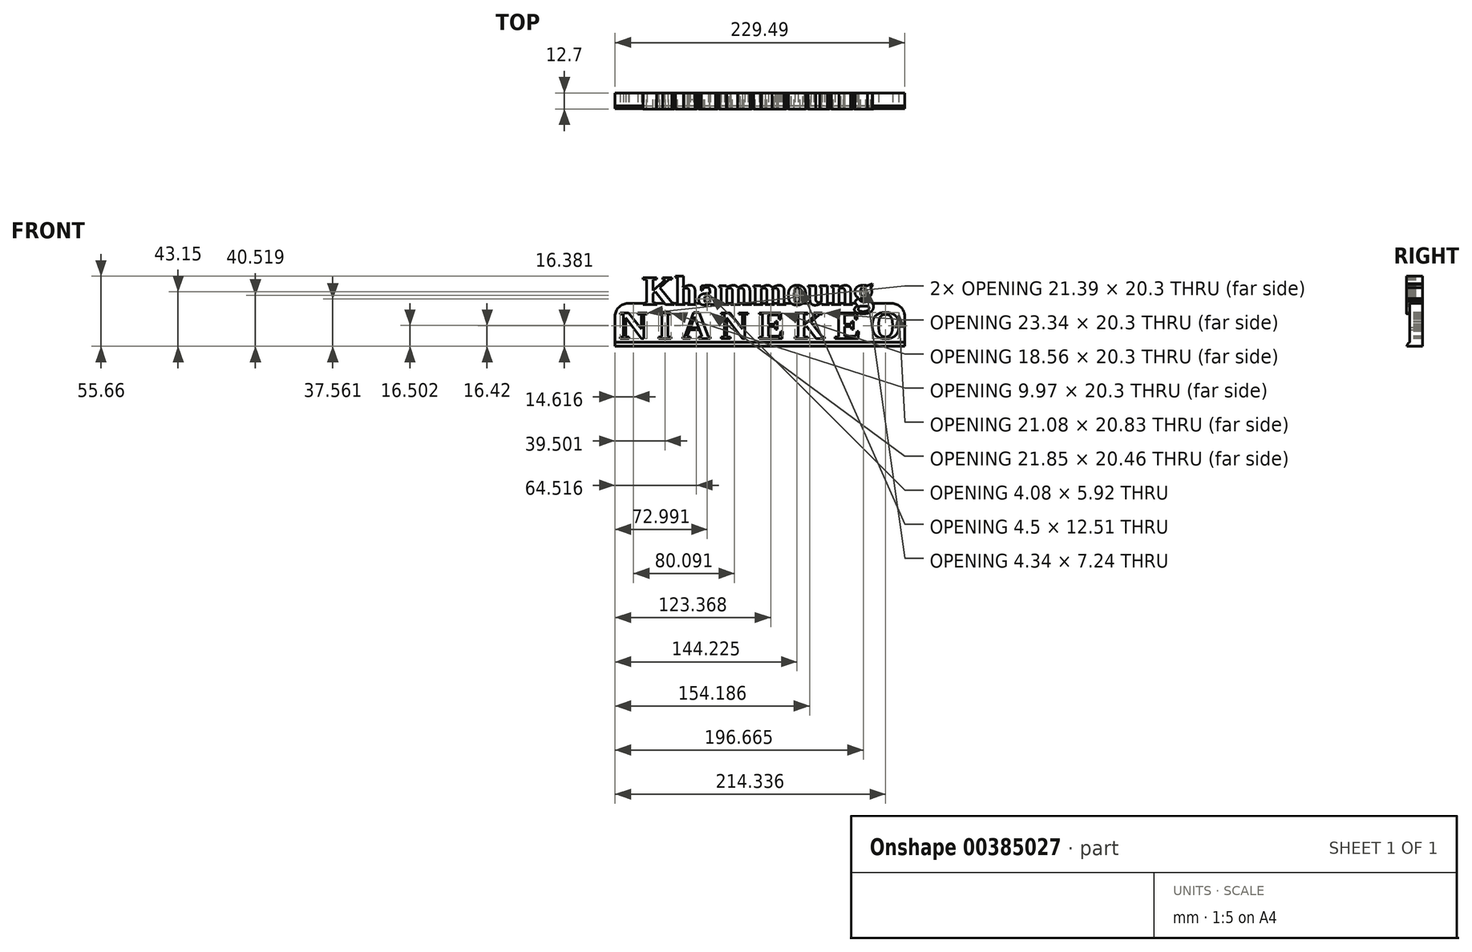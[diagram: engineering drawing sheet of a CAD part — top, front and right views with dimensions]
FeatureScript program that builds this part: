
annotation { "Feature Type Name" : "Feature", "Feature Type Description" : "" }
export const myFeature = defineFeature(function(context is Context, id is Id, definition is map)
    precondition{}
    {
        {
            var Q0;
            Q0=qCreatedBy(makeId("Front.planeOp"),FACE);
            var sketch = newSketch(context, id + "F0", { "sketchPlane" : qUnion([Q0])});
            skLineSegment(sketch, "E0.bottom", {"start": v(-114.42, 5.35) * mm, "end": v(115.07, 5.35) * mm});
            skLineSegment(sketch, "E0.top", {"start": v(-114.42, -28.6) * mm, "end": v(115.07, -28.6) * mm});
            skLineSegment(sketch, "E0.left", {"start": v(-114.42, 5.35) * mm, "end": v(-114.42, -28.6) * mm});
            skLineSegment(sketch, "E0.right", {"start": v(115.07, 5.35) * mm, "end": v(115.07, -28.6) * mm});
            skSolve(sketch);
        }
        {
            var Q0;
            Q0 = qSketchRegion(id + "F0", true);
            extrude(context, id + "F1", {"entities" : qUnion([Q0]), "depth" : 10.16 * mm});
        }
        {
            var Q0;
            Q0=qCreatedBy(makeId("Front.planeOp"),FACE);
            var sketch = newSketch(context, id + "F2", { "sketchPlane" : qUnion([Q0])});
            skText(sketch, "E1", { "text": "Khammoung", "fontName": "Tinos-Bold.ttf"});
            const initialGuessF2  = {"E1": [-0.09269, 0.0044, 1, 0, 0.02352]};
            skSetInitialGuess(sketch, initialGuessF2);
            skSolve(sketch);
        }
        {
            var Q0;
            Q0 = qSketchRegion(id + "F2", true);
            extrude(context, id + "F3", {"entities" : qUnion([Q0]), "operationType" : NewBodyOperationType.ADD, "depth" : 12.7 * mm});
        }
        {
            var Q0;
            {var subQ0=sQuery(id+"F0.wireOp",EDGE,"E0.bottom");var subQ1=sQuery(id+"F0.wireOp",EDGE,"E0.top");var subQ2=sQuery(id+"F0.wireOp",EDGE,"E0.left");var subQ3=sQuery(id+"F0.wireOp",EDGE,"E0.right");Q0=makeQuery(id+"F3.boolean.opBoolean","SPLIT",FACE,{"disambiguationData":[TD([makeQuery(id+"F1.opExtrude","SWEPT_FACE",FACE,{"disambiguationData":[OSD([subQ1])]})])],"derivedFrom":makeQuery(id+"F1.opExtrude","CAP_FACE",FACE,{"disambiguationData":[OSD([subQ0,subQ1,subQ2,subQ3])],"isStart":false})});}
            var sketch = newSketch(context, id + "F4", { "sketchPlane" : qUnion([Q0])});
            skLineSegment(sketch, "E2.bottom", {"start": v(-114.42, -28.6) * mm, "end": v(115.07, -28.6) * mm});
            skLineSegment(sketch, "E2.top", {"start": v(-114.42, -25.32) * mm, "end": v(115.07, -25.32) * mm});
            skLineSegment(sketch, "E2.left", {"start": v(-114.42, -28.6) * mm, "end": v(-114.42, -25.32) * mm});
            skLineSegment(sketch, "E2.right", {"start": v(115.07, -28.6) * mm, "end": v(115.07, -25.32) * mm});
            skSolve(sketch);
        }
        {
            var Q0;
            Q0 = qSketchRegion(id + "F4", true);
            extrude(context, id + "F5", {"entities" : qUnion([Q0]), "operationType" : NewBodyOperationType.ADD, "depth" : 2.54 * mm});
        }
        {
            var Q0;
            Q0=makeQuery(id+"F5.opExtrude","CAP_EDGE",EDGE,{"disambiguationData":[OSD([sQuery(id+"F4.wireOp",EDGE,"E2.top")])],"isStart":false});
            fillet(context, id + "F6", {"entities" : qUnion([Q0]), "radius" : 5.08 * mm, "tangentPropagation" : true, "allowEdgeOverflow" : false});
        }
        {
            var Q0;
            {var subQ0=sQuery(id+"F0.wireOp",EDGE,"E0.bottom");var subQ1=sQuery(id+"F0.wireOp",EDGE,"E0.right");var subQ2=sQuery(id+"F0.wireOp",EDGE,"E0.top");var subQ3=sQuery(id+"F0.wireOp",EDGE,"E0.left");Q0=makeQuery(id+"F3.boolean.opBoolean","SPLIT",FACE,{"disambiguationData":[TD([makeQuery(id+"F1.opExtrude","SWEPT_FACE",FACE,{"disambiguationData":[OSD([subQ2])]})])],"derivedFrom":makeQuery(id+"F1.opExtrude","CAP_FACE",FACE,{"disambiguationData":[OSD([subQ0,subQ2,subQ3,subQ1])],"isStart":false})});}
            var sketch = newSketch(context, id + "F7", { "sketchPlane" : qUnion([Q0])});
            skText(sketch, "E3", { "text": "N I A N E K E O", "fontName": "Tinos-Bold.ttf"});
            const initialGuessF7  = {"E3": [-0.11109, -0.02232, 1, 0, 0.02232]};
            skSetInitialGuess(sketch, initialGuessF7);
            skSolve(sketch);
        }
        {
            var Q0;
            Q0 = qSketchRegion(id + "F7", true);
            var Q1;
            Q1=makeQuery(id+"F3.boolean.opBoolean","MERGE",FACE,{"derivedFrom":[makeQuery(id+"F1.opExtrude","CAP_FACE",FACE,{"disambiguationData":[OSD([sQuery(id+"F0.wireOp",EDGE,"E0.bottom"),sQuery(id+"F0.wireOp",EDGE,"E0.top"),sQuery(id+"F0.wireOp",EDGE,"E0.left"),sQuery(id+"F0.wireOp",EDGE,"E0.right")])],"isStart":true}),makeQuery(id+"F3.opExtrude","CAP_FACE",FACE,{"disambiguationData":[OSD([sQuery(id+"F2.wireOp",EDGE,"E1.sketch_text.stroke-0"),sQuery(id+"F2.wireOp",EDGE,"E1.sketch_text.stroke-1"),sQuery(id+"F2.wireOp",EDGE,"E1.sketch_text.stroke-2"),sQuery(id+"F2.wireOp",EDGE,"E1.sketch_text.stroke-3"),sQuery(id+"F2.wireOp",EDGE,"E1.sketch_text.stroke-4"),sQuery(id+"F2.wireOp",EDGE,"E1.sketch_text.stroke-5"),sQuery(id+"F2.wireOp",EDGE,"E1.sketch_text.stroke-6"),sQuery(id+"F2.wireOp",EDGE,"E1.sketch_text.stroke-7"),sQuery(id+"F2.wireOp",EDGE,"E1.sketch_text.stroke-8"),sQuery(id+"F2.wireOp",EDGE,"E1.sketch_text.stroke-9"),sQuery(id+"F2.wireOp",EDGE,"E1.sketch_text.stroke-10"),sQuery(id+"F2.wireOp",EDGE,"E1.sketch_text.stroke-11"),sQuery(id+"F2.wireOp",EDGE,"E1.sketch_text.stroke-12"),sQuery(id+"F2.wireOp",EDGE,"E1.sketch_text.stroke-13"),sQuery(id+"F2.wireOp",EDGE,"E1.sketch_text.stroke-14"),sQuery(id+"F2.wireOp",EDGE,"E1.sketch_text.stroke-15"),sQuery(id+"F2.wireOp",EDGE,"E1.sketch_text.stroke-16"),sQuery(id+"F2.wireOp",EDGE,"E1.sketch_text.stroke-17"),sQuery(id+"F2.wireOp",EDGE,"E1.sketch_text.stroke-18"),sQuery(id+"F2.wireOp",EDGE,"E1.sketch_text.stroke-19"),sQuery(id+"F2.wireOp",EDGE,"E1.sketch_text.stroke-20"),sQuery(id+"F2.wireOp",EDGE,"E1.sketch_text.stroke-21"),sQuery(id+"F2.wireOp",EDGE,"E1.sketch_text.stroke-22"),sQuery(id+"F2.wireOp",EDGE,"E1.sketch_text.stroke-23"),sQuery(id+"F2.wireOp",EDGE,"E1.sketch_text.stroke-24"),sQuery(id+"F2.wireOp",EDGE,"E1.sketch_text.stroke-25")])],"isStart":true}),makeQuery(id+"F3.opExtrude","CAP_FACE",FACE,{"disambiguationData":[OSD([sQuery(id+"F2.wireOp",EDGE,"E1.sketch_text.stroke-26"),sQuery(id+"F2.wireOp",EDGE,"E1.sketch_text.stroke-27"),sQuery(id+"F2.wireOp",EDGE,"E1.sketch_text.stroke-28"),sQuery(id+"F2.wireOp",EDGE,"E1.sketch_text.stroke-29"),sQuery(id+"F2.wireOp",EDGE,"E1.sketch_text.stroke-30"),sQuery(id+"F2.wireOp",EDGE,"E1.sketch_text.stroke-31"),sQuery(id+"F2.wireOp",EDGE,"E1.sketch_text.stroke-32"),sQuery(id+"F2.wireOp",EDGE,"E1.sketch_text.stroke-33"),sQuery(id+"F2.wireOp",EDGE,"E1.sketch_text.stroke-34"),sQuery(id+"F2.wireOp",EDGE,"E1.sketch_text.stroke-35"),sQuery(id+"F2.wireOp",EDGE,"E1.sketch_text.stroke-36"),sQuery(id+"F2.wireOp",EDGE,"E1.sketch_text.stroke-37"),sQuery(id+"F2.wireOp",EDGE,"E1.sketch_text.stroke-38"),sQuery(id+"F2.wireOp",EDGE,"E1.sketch_text.stroke-39"),sQuery(id+"F2.wireOp",EDGE,"E1.sketch_text.stroke-40"),sQuery(id+"F2.wireOp",EDGE,"E1.sketch_text.stroke-41"),sQuery(id+"F2.wireOp",EDGE,"E1.sketch_text.stroke-42"),sQuery(id+"F2.wireOp",EDGE,"E1.sketch_text.stroke-43"),sQuery(id+"F2.wireOp",EDGE,"E1.sketch_text.stroke-44"),sQuery(id+"F2.wireOp",EDGE,"E1.sketch_text.stroke-45"),sQuery(id+"F2.wireOp",EDGE,"E1.sketch_text.stroke-46"),sQuery(id+"F2.wireOp",EDGE,"E1.sketch_text.stroke-47"),sQuery(id+"F2.wireOp",EDGE,"E1.sketch_text.stroke-48"),sQuery(id+"F2.wireOp",EDGE,"E1.sketch_text.stroke-49"),sQuery(id+"F2.wireOp",EDGE,"E1.sketch_text.stroke-50")])],"isStart":true}),makeQuery(id+"F3.opExtrude","CAP_FACE",FACE,{"disambiguationData":[OSD([sQuery(id+"F2.wireOp",EDGE,"E1.sketch_text.stroke-51"),sQuery(id+"F2.wireOp",EDGE,"E1.sketch_text.stroke-52"),sQuery(id+"F2.wireOp",EDGE,"E1.sketch_text.stroke-53"),sQuery(id+"F2.wireOp",EDGE,"E1.sketch_text.stroke-54"),sQuery(id+"F2.wireOp",EDGE,"E1.sketch_text.stroke-55"),sQuery(id+"F2.wireOp",EDGE,"E1.sketch_text.stroke-56"),sQuery(id+"F2.wireOp",EDGE,"E1.sketch_text.stroke-57"),sQuery(id+"F2.wireOp",EDGE,"E1.sketch_text.stroke-58"),sQuery(id+"F2.wireOp",EDGE,"E1.sketch_text.stroke-59"),sQuery(id+"F2.wireOp",EDGE,"E1.sketch_text.stroke-60"),sQuery(id+"F2.wireOp",EDGE,"E1.sketch_text.stroke-61"),sQuery(id+"F2.wireOp",EDGE,"E1.sketch_text.stroke-62"),sQuery(id+"F2.wireOp",EDGE,"E1.sketch_text.stroke-63"),sQuery(id+"F2.wireOp",EDGE,"E1.sketch_text.stroke-64"),sQuery(id+"F2.wireOp",EDGE,"E1.sketch_text.stroke-65"),sQuery(id+"F2.wireOp",EDGE,"E1.sketch_text.stroke-66"),sQuery(id+"F2.wireOp",EDGE,"E1.sketch_text.stroke-67"),sQuery(id+"F2.wireOp",EDGE,"E1.sketch_text.stroke-68"),sQuery(id+"F2.wireOp",EDGE,"E1.sketch_text.stroke-69"),sQuery(id+"F2.wireOp",EDGE,"E1.sketch_text.stroke-70"),sQuery(id+"F2.wireOp",EDGE,"E1.sketch_text.stroke-71"),sQuery(id+"F2.wireOp",EDGE,"E1.sketch_text.stroke-72"),sQuery(id+"F2.wireOp",EDGE,"E1.sketch_text.stroke-73"),sQuery(id+"F2.wireOp",EDGE,"E1.sketch_text.stroke-74"),sQuery(id+"F2.wireOp",EDGE,"E1.sketch_text.stroke-75"),sQuery(id+"F2.wireOp",EDGE,"E1.sketch_text.stroke-76"),sQuery(id+"F2.wireOp",EDGE,"E1.sketch_text.stroke-77"),sQuery(id+"F2.wireOp",EDGE,"E1.sketch_text.stroke-78")])],"isStart":true}),makeQuery(id+"F3.opExtrude","CAP_FACE",FACE,{"disambiguationData":[OSD([sQuery(id+"F2.wireOp",EDGE,"E1.sketch_text.stroke-79"),sQuery(id+"F2.wireOp",EDGE,"E1.sketch_text.stroke-80"),sQuery(id+"F2.wireOp",EDGE,"E1.sketch_text.stroke-81"),sQuery(id+"F2.wireOp",EDGE,"E1.sketch_text.stroke-82"),sQuery(id+"F2.wireOp",EDGE,"E1.sketch_text.stroke-83"),sQuery(id+"F2.wireOp",EDGE,"E1.sketch_text.stroke-84"),sQuery(id+"F2.wireOp",EDGE,"E1.sketch_text.stroke-85"),sQuery(id+"F2.wireOp",EDGE,"E1.sketch_text.stroke-86"),sQuery(id+"F2.wireOp",EDGE,"E1.sketch_text.stroke-87"),sQuery(id+"F2.wireOp",EDGE,"E1.sketch_text.stroke-88"),sQuery(id+"F2.wireOp",EDGE,"E1.sketch_text.stroke-89"),sQuery(id+"F2.wireOp",EDGE,"E1.sketch_text.stroke-90"),sQuery(id+"F2.wireOp",EDGE,"E1.sketch_text.stroke-91"),sQuery(id+"F2.wireOp",EDGE,"E1.sketch_text.stroke-92"),sQuery(id+"F2.wireOp",EDGE,"E1.sketch_text.stroke-93"),sQuery(id+"F2.wireOp",EDGE,"E1.sketch_text.stroke-94"),sQuery(id+"F2.wireOp",EDGE,"E1.sketch_text.stroke-95"),sQuery(id+"F2.wireOp",EDGE,"E1.sketch_text.stroke-96"),sQuery(id+"F2.wireOp",EDGE,"E1.sketch_text.stroke-97"),sQuery(id+"F2.wireOp",EDGE,"E1.sketch_text.stroke-98"),sQuery(id+"F2.wireOp",EDGE,"E1.sketch_text.stroke-99"),sQuery(id+"F2.wireOp",EDGE,"E1.sketch_text.stroke-100"),sQuery(id+"F2.wireOp",EDGE,"E1.sketch_text.stroke-101"),sQuery(id+"F2.wireOp",EDGE,"E1.sketch_text.stroke-102"),sQuery(id+"F2.wireOp",EDGE,"E1.sketch_text.stroke-103"),sQuery(id+"F2.wireOp",EDGE,"E1.sketch_text.stroke-104"),sQuery(id+"F2.wireOp",EDGE,"E1.sketch_text.stroke-105"),sQuery(id+"F2.wireOp",EDGE,"E1.sketch_text.stroke-106"),sQuery(id+"F2.wireOp",EDGE,"E1.sketch_text.stroke-107"),sQuery(id+"F2.wireOp",EDGE,"E1.sketch_text.stroke-108"),sQuery(id+"F2.wireOp",EDGE,"E1.sketch_text.stroke-109"),sQuery(id+"F2.wireOp",EDGE,"E1.sketch_text.stroke-110"),sQuery(id+"F2.wireOp",EDGE,"E1.sketch_text.stroke-111"),sQuery(id+"F2.wireOp",EDGE,"E1.sketch_text.stroke-112"),sQuery(id+"F2.wireOp",EDGE,"E1.sketch_text.stroke-113"),sQuery(id+"F2.wireOp",EDGE,"E1.sketch_text.stroke-114"),sQuery(id+"F2.wireOp",EDGE,"E1.sketch_text.stroke-115")])],"isStart":true}),makeQuery(id+"F3.opExtrude","CAP_FACE",FACE,{"disambiguationData":[OSD([sQuery(id+"F2.wireOp",EDGE,"E1.sketch_text.stroke-116"),sQuery(id+"F2.wireOp",EDGE,"E1.sketch_text.stroke-117"),sQuery(id+"F2.wireOp",EDGE,"E1.sketch_text.stroke-118"),sQuery(id+"F2.wireOp",EDGE,"E1.sketch_text.stroke-119"),sQuery(id+"F2.wireOp",EDGE,"E1.sketch_text.stroke-120"),sQuery(id+"F2.wireOp",EDGE,"E1.sketch_text.stroke-121"),sQuery(id+"F2.wireOp",EDGE,"E1.sketch_text.stroke-122"),sQuery(id+"F2.wireOp",EDGE,"E1.sketch_text.stroke-123"),sQuery(id+"F2.wireOp",EDGE,"E1.sketch_text.stroke-124"),sQuery(id+"F2.wireOp",EDGE,"E1.sketch_text.stroke-125"),sQuery(id+"F2.wireOp",EDGE,"E1.sketch_text.stroke-126"),sQuery(id+"F2.wireOp",EDGE,"E1.sketch_text.stroke-127"),sQuery(id+"F2.wireOp",EDGE,"E1.sketch_text.stroke-128"),sQuery(id+"F2.wireOp",EDGE,"E1.sketch_text.stroke-129"),sQuery(id+"F2.wireOp",EDGE,"E1.sketch_text.stroke-130"),sQuery(id+"F2.wireOp",EDGE,"E1.sketch_text.stroke-131"),sQuery(id+"F2.wireOp",EDGE,"E1.sketch_text.stroke-132"),sQuery(id+"F2.wireOp",EDGE,"E1.sketch_text.stroke-133"),sQuery(id+"F2.wireOp",EDGE,"E1.sketch_text.stroke-134"),sQuery(id+"F2.wireOp",EDGE,"E1.sketch_text.stroke-135"),sQuery(id+"F2.wireOp",EDGE,"E1.sketch_text.stroke-136"),sQuery(id+"F2.wireOp",EDGE,"E1.sketch_text.stroke-137"),sQuery(id+"F2.wireOp",EDGE,"E1.sketch_text.stroke-138"),sQuery(id+"F2.wireOp",EDGE,"E1.sketch_text.stroke-139"),sQuery(id+"F2.wireOp",EDGE,"E1.sketch_text.stroke-140"),sQuery(id+"F2.wireOp",EDGE,"E1.sketch_text.stroke-141"),sQuery(id+"F2.wireOp",EDGE,"E1.sketch_text.stroke-142"),sQuery(id+"F2.wireOp",EDGE,"E1.sketch_text.stroke-143"),sQuery(id+"F2.wireOp",EDGE,"E1.sketch_text.stroke-144"),sQuery(id+"F2.wireOp",EDGE,"E1.sketch_text.stroke-145"),sQuery(id+"F2.wireOp",EDGE,"E1.sketch_text.stroke-146"),sQuery(id+"F2.wireOp",EDGE,"E1.sketch_text.stroke-147"),sQuery(id+"F2.wireOp",EDGE,"E1.sketch_text.stroke-148"),sQuery(id+"F2.wireOp",EDGE,"E1.sketch_text.stroke-149"),sQuery(id+"F2.wireOp",EDGE,"E1.sketch_text.stroke-150"),sQuery(id+"F2.wireOp",EDGE,"E1.sketch_text.stroke-151"),sQuery(id+"F2.wireOp",EDGE,"E1.sketch_text.stroke-152")])],"isStart":true}),makeQuery(id+"F3.opExtrude","CAP_FACE",FACE,{"disambiguationData":[OSD([sQuery(id+"F2.wireOp",EDGE,"E1.sketch_text.stroke-153"),sQuery(id+"F2.wireOp",EDGE,"E1.sketch_text.stroke-154"),sQuery(id+"F2.wireOp",EDGE,"E1.sketch_text.stroke-155"),sQuery(id+"F2.wireOp",EDGE,"E1.sketch_text.stroke-156"),sQuery(id+"F2.wireOp",EDGE,"E1.sketch_text.stroke-157"),sQuery(id+"F2.wireOp",EDGE,"E1.sketch_text.stroke-158"),sQuery(id+"F2.wireOp",EDGE,"E1.sketch_text.stroke-159"),sQuery(id+"F2.wireOp",EDGE,"E1.sketch_text.stroke-160"),sQuery(id+"F2.wireOp",EDGE,"E1.sketch_text.stroke-161"),sQuery(id+"F2.wireOp",EDGE,"E1.sketch_text.stroke-162"),sQuery(id+"F2.wireOp",EDGE,"E1.sketch_text.stroke-163"),sQuery(id+"F2.wireOp",EDGE,"E1.sketch_text.stroke-164"),sQuery(id+"F2.wireOp",EDGE,"E1.sketch_text.stroke-165"),sQuery(id+"F2.wireOp",EDGE,"E1.sketch_text.stroke-166"),sQuery(id+"F2.wireOp",EDGE,"E1.sketch_text.stroke-167"),sQuery(id+"F2.wireOp",EDGE,"E1.sketch_text.stroke-168")])],"isStart":true}),makeQuery(id+"F3.opExtrude","CAP_FACE",FACE,{"disambiguationData":[OSD([sQuery(id+"F2.wireOp",EDGE,"E1.sketch_text.stroke-169"),sQuery(id+"F2.wireOp",EDGE,"E1.sketch_text.stroke-170"),sQuery(id+"F2.wireOp",EDGE,"E1.sketch_text.stroke-171"),sQuery(id+"F2.wireOp",EDGE,"E1.sketch_text.stroke-172"),sQuery(id+"F2.wireOp",EDGE,"E1.sketch_text.stroke-173"),sQuery(id+"F2.wireOp",EDGE,"E1.sketch_text.stroke-174"),sQuery(id+"F2.wireOp",EDGE,"E1.sketch_text.stroke-175"),sQuery(id+"F2.wireOp",EDGE,"E1.sketch_text.stroke-176"),sQuery(id+"F2.wireOp",EDGE,"E1.sketch_text.stroke-177"),sQuery(id+"F2.wireOp",EDGE,"E1.sketch_text.stroke-178"),sQuery(id+"F2.wireOp",EDGE,"E1.sketch_text.stroke-179"),sQuery(id+"F2.wireOp",EDGE,"E1.sketch_text.stroke-180"),sQuery(id+"F2.wireOp",EDGE,"E1.sketch_text.stroke-181"),sQuery(id+"F2.wireOp",EDGE,"E1.sketch_text.stroke-182"),sQuery(id+"F2.wireOp",EDGE,"E1.sketch_text.stroke-183"),sQuery(id+"F2.wireOp",EDGE,"E1.sketch_text.stroke-184"),sQuery(id+"F2.wireOp",EDGE,"E1.sketch_text.stroke-185"),sQuery(id+"F2.wireOp",EDGE,"E1.sketch_text.stroke-186"),sQuery(id+"F2.wireOp",EDGE,"E1.sketch_text.stroke-187"),sQuery(id+"F2.wireOp",EDGE,"E1.sketch_text.stroke-188")])],"isStart":true}),makeQuery(id+"F3.opExtrude","CAP_FACE",FACE,{"disambiguationData":[OSD([sQuery(id+"F2.wireOp",EDGE,"E1.sketch_text.stroke-189"),sQuery(id+"F2.wireOp",EDGE,"E1.sketch_text.stroke-190"),sQuery(id+"F2.wireOp",EDGE,"E1.sketch_text.stroke-191"),sQuery(id+"F2.wireOp",EDGE,"E1.sketch_text.stroke-192"),sQuery(id+"F2.wireOp",EDGE,"E1.sketch_text.stroke-193"),sQuery(id+"F2.wireOp",EDGE,"E1.sketch_text.stroke-194"),sQuery(id+"F2.wireOp",EDGE,"E1.sketch_text.stroke-195"),sQuery(id+"F2.wireOp",EDGE,"E1.sketch_text.stroke-196"),sQuery(id+"F2.wireOp",EDGE,"E1.sketch_text.stroke-197"),sQuery(id+"F2.wireOp",EDGE,"E1.sketch_text.stroke-198"),sQuery(id+"F2.wireOp",EDGE,"E1.sketch_text.stroke-199"),sQuery(id+"F2.wireOp",EDGE,"E1.sketch_text.stroke-200"),sQuery(id+"F2.wireOp",EDGE,"E1.sketch_text.stroke-201"),sQuery(id+"F2.wireOp",EDGE,"E1.sketch_text.stroke-202"),sQuery(id+"F2.wireOp",EDGE,"E1.sketch_text.stroke-203"),sQuery(id+"F2.wireOp",EDGE,"E1.sketch_text.stroke-204"),sQuery(id+"F2.wireOp",EDGE,"E1.sketch_text.stroke-205"),sQuery(id+"F2.wireOp",EDGE,"E1.sketch_text.stroke-206"),sQuery(id+"F2.wireOp",EDGE,"E1.sketch_text.stroke-207"),sQuery(id+"F2.wireOp",EDGE,"E1.sketch_text.stroke-208"),sQuery(id+"F2.wireOp",EDGE,"E1.sketch_text.stroke-209"),sQuery(id+"F2.wireOp",EDGE,"E1.sketch_text.stroke-210"),sQuery(id+"F2.wireOp",EDGE,"E1.sketch_text.stroke-211"),sQuery(id+"F2.wireOp",EDGE,"E1.sketch_text.stroke-212")])],"isStart":true}),makeQuery(id+"F3.opExtrude","CAP_FACE",FACE,{"disambiguationData":[OSD([sQuery(id+"F2.wireOp",EDGE,"E1.sketch_text.stroke-213"),sQuery(id+"F2.wireOp",EDGE,"E1.sketch_text.stroke-214"),sQuery(id+"F2.wireOp",EDGE,"E1.sketch_text.stroke-215"),sQuery(id+"F2.wireOp",EDGE,"E1.sketch_text.stroke-216"),sQuery(id+"F2.wireOp",EDGE,"E1.sketch_text.stroke-217"),sQuery(id+"F2.wireOp",EDGE,"E1.sketch_text.stroke-218"),sQuery(id+"F2.wireOp",EDGE,"E1.sketch_text.stroke-219"),sQuery(id+"F2.wireOp",EDGE,"E1.sketch_text.stroke-220"),sQuery(id+"F2.wireOp",EDGE,"E1.sketch_text.stroke-221"),sQuery(id+"F2.wireOp",EDGE,"E1.sketch_text.stroke-222"),sQuery(id+"F2.wireOp",EDGE,"E1.sketch_text.stroke-223"),sQuery(id+"F2.wireOp",EDGE,"E1.sketch_text.stroke-224"),sQuery(id+"F2.wireOp",EDGE,"E1.sketch_text.stroke-225"),sQuery(id+"F2.wireOp",EDGE,"E1.sketch_text.stroke-226"),sQuery(id+"F2.wireOp",EDGE,"E1.sketch_text.stroke-227"),sQuery(id+"F2.wireOp",EDGE,"E1.sketch_text.stroke-228"),sQuery(id+"F2.wireOp",EDGE,"E1.sketch_text.stroke-229"),sQuery(id+"F2.wireOp",EDGE,"E1.sketch_text.stroke-230"),sQuery(id+"F2.wireOp",EDGE,"E1.sketch_text.stroke-231"),sQuery(id+"F2.wireOp",EDGE,"E1.sketch_text.stroke-232"),sQuery(id+"F2.wireOp",EDGE,"E1.sketch_text.stroke-233"),sQuery(id+"F2.wireOp",EDGE,"E1.sketch_text.stroke-234"),sQuery(id+"F2.wireOp",EDGE,"E1.sketch_text.stroke-235"),sQuery(id+"F2.wireOp",EDGE,"E1.sketch_text.stroke-236"),sQuery(id+"F2.wireOp",EDGE,"E1.sketch_text.stroke-237"),sQuery(id+"F2.wireOp",EDGE,"E1.sketch_text.stroke-238"),sQuery(id+"F2.wireOp",EDGE,"E1.sketch_text.stroke-239"),sQuery(id+"F2.wireOp",EDGE,"E1.sketch_text.stroke-240"),sQuery(id+"F2.wireOp",EDGE,"E1.sketch_text.stroke-241"),sQuery(id+"F2.wireOp",EDGE,"E1.sketch_text.stroke-242"),sQuery(id+"F2.wireOp",EDGE,"E1.sketch_text.stroke-243"),sQuery(id+"F2.wireOp",EDGE,"E1.sketch_text.stroke-244"),sQuery(id+"F2.wireOp",EDGE,"E1.sketch_text.stroke-245"),sQuery(id+"F2.wireOp",EDGE,"E1.sketch_text.stroke-246"),sQuery(id+"F2.wireOp",EDGE,"E1.sketch_text.stroke-247"),sQuery(id+"F2.wireOp",EDGE,"E1.sketch_text.stroke-248"),sQuery(id+"F2.wireOp",EDGE,"E1.sketch_text.stroke-249"),sQuery(id+"F2.wireOp",EDGE,"E1.sketch_text.stroke-250"),sQuery(id+"F2.wireOp",EDGE,"E1.sketch_text.stroke-251"),sQuery(id+"F2.wireOp",EDGE,"E1.sketch_text.stroke-252"),sQuery(id+"F2.wireOp",EDGE,"E1.sketch_text.stroke-253"),sQuery(id+"F2.wireOp",EDGE,"E1.sketch_text.stroke-254")])],"isStart":true})]});
            extrude(context, id + "F8", {"entities" : qUnion([Q0]), "operationType" : NewBodyOperationType.REMOVE, "endBound" : BoundingType.UP_TO_SURFACE, "oppositeDirection" : true, "endBoundEntityFace" : qUnion([Q1]), "depth" : 25.4 * mm});
        }
        {
            var Q0;
            Q0=makeQuery(id+"F1.opExtrude","SWEPT_EDGE",EDGE,{"disambiguationData":[OSD([sQuery(id+"F0.wireOp",EDGE,"E0.bottom"),sQuery(id+"F0.wireOp",EDGE,"E0.left")])]});
            var Q1;
            Q1=makeQuery(id+"F1.opExtrude","SWEPT_EDGE",EDGE,{"disambiguationData":[OSD([sQuery(id+"F0.wireOp",EDGE,"E0.bottom"),sQuery(id+"F0.wireOp",EDGE,"E0.right")])]});
            fillet(context, id + "F9", {"entities" : qUnion([Q0, Q1]), "radius" : 10.16 * mm, "tangentPropagation" : true, "allowEdgeOverflow" : false});
        }
        {
            var Q0;
            {var subQ0=sQuery(id+"F2.wireOp",EDGE,"E1.sketch_text.stroke-238");var subQ1=sQuery(id+"F2.wireOp",EDGE,"E1.sketch_text.stroke-229");var subQ2=sQuery(id+"F2.wireOp",EDGE,"E1.sketch_text.stroke-228");var subQ3=sQuery(id+"F2.wireOp",EDGE,"E1.sketch_text.stroke-227");var subQ4=sQuery(id+"F2.wireOp",EDGE,"E1.sketch_text.stroke-219");var subQ5=sQuery(id+"F2.wireOp",EDGE,"E1.sketch_text.stroke-218");var subQ6=sQuery(id+"F2.wireOp",EDGE,"E1.sketch_text.stroke-217");var subQ7=sQuery(id+"F2.wireOp",EDGE,"E1.sketch_text.stroke-213");var subQ8=sQuery(id+"F2.wireOp",EDGE,"E1.sketch_text.stroke-212");var subQ9=sQuery(id+"F2.wireOp",EDGE,"E1.sketch_text.stroke-198");var subQ10=sQuery(id+"F2.wireOp",EDGE,"E1.sketch_text.stroke-197");var subQ11=sQuery(id+"F2.wireOp",EDGE,"E1.sketch_text.stroke-191");var subQ12=sQuery(id+"F2.wireOp",EDGE,"E1.sketch_text.stroke-190");var subQ13=sQuery(id+"F2.wireOp",EDGE,"E1.sketch_text.stroke-184");var subQ14=sQuery(id+"F2.wireOp",EDGE,"E1.sketch_text.stroke-183");var subQ15=sQuery(id+"F2.wireOp",EDGE,"E1.sketch_text.stroke-182");var subQ16=sQuery(id+"F2.wireOp",EDGE,"E1.sketch_text.stroke-181");var subQ17=sQuery(id+"F2.wireOp",EDGE,"E1.sketch_text.stroke-180");var subQ18=sQuery(id+"F2.wireOp",EDGE,"E1.sketch_text.stroke-179");var subQ19=sQuery(id+"F2.wireOp",EDGE,"E1.sketch_text.stroke-178");var subQ20=sQuery(id+"F2.wireOp",EDGE,"E1.sketch_text.stroke-177");var subQ21=sQuery(id+"F2.wireOp",EDGE,"E1.sketch_text.stroke-176");var subQ22=sQuery(id+"F2.wireOp",EDGE,"E1.sketch_text.stroke-175");var subQ23=sQuery(id+"F2.wireOp",EDGE,"E1.sketch_text.stroke-174");var subQ24=sQuery(id+"F2.wireOp",EDGE,"E1.sketch_text.stroke-173");var subQ25=sQuery(id+"F2.wireOp",EDGE,"E1.sketch_text.stroke-172");var subQ26=sQuery(id+"F2.wireOp",EDGE,"E1.sketch_text.stroke-171");var subQ27=sQuery(id+"F2.wireOp",EDGE,"E1.sketch_text.stroke-169");var subQ28=sQuery(id+"F2.wireOp",EDGE,"E1.sketch_text.stroke-168");var subQ29=sQuery(id+"F2.wireOp",EDGE,"E1.sketch_text.stroke-167");var subQ30=sQuery(id+"F2.wireOp",EDGE,"E1.sketch_text.stroke-166");var subQ31=sQuery(id+"F2.wireOp",EDGE,"E1.sketch_text.stroke-162");var subQ32=sQuery(id+"F2.wireOp",EDGE,"E1.sketch_text.stroke-161");var subQ33=sQuery(id+"F2.wireOp",EDGE,"E1.sketch_text.stroke-159");var subQ34=sQuery(id+"F2.wireOp",EDGE,"E1.sketch_text.stroke-158");var subQ35=sQuery(id+"F2.wireOp",EDGE,"E1.sketch_text.stroke-157");var subQ36=sQuery(id+"F2.wireOp",EDGE,"E1.sketch_text.stroke-156");var subQ37=sQuery(id+"F2.wireOp",EDGE,"E1.sketch_text.stroke-155");var subQ38=sQuery(id+"F2.wireOp",EDGE,"E1.sketch_text.stroke-154");var subQ39=sQuery(id+"F2.wireOp",EDGE,"E1.sketch_text.stroke-153");var subQ40=sQuery(id+"F2.wireOp",EDGE,"E1.sketch_text.stroke-152");var subQ41=sQuery(id+"F2.wireOp",EDGE,"E1.sketch_text.stroke-151");var subQ42=sQuery(id+"F2.wireOp",EDGE,"E1.sketch_text.stroke-150");var subQ43=sQuery(id+"F2.wireOp",EDGE,"E1.sketch_text.stroke-149");var subQ44=sQuery(id+"F2.wireOp",EDGE,"E1.sketch_text.stroke-148");var subQ45=sQuery(id+"F2.wireOp",EDGE,"E1.sketch_text.stroke-147");var subQ46=sQuery(id+"F2.wireOp",EDGE,"E1.sketch_text.stroke-143");var subQ47=sQuery(id+"F2.wireOp",EDGE,"E1.sketch_text.stroke-142");var subQ48=sQuery(id+"F2.wireOp",EDGE,"E1.sketch_text.stroke-141");var subQ49=sQuery(id+"F2.wireOp",EDGE,"E1.sketch_text.stroke-140");var subQ50=sQuery(id+"F2.wireOp",EDGE,"E1.sketch_text.stroke-139");var subQ51=sQuery(id+"F2.wireOp",EDGE,"E1.sketch_text.stroke-138");var subQ52=sQuery(id+"F2.wireOp",EDGE,"E1.sketch_text.stroke-137");var subQ53=sQuery(id+"F2.wireOp",EDGE,"E1.sketch_text.stroke-133");var subQ54=sQuery(id+"F2.wireOp",EDGE,"E1.sketch_text.stroke-132");var subQ55=sQuery(id+"F2.wireOp",EDGE,"E1.sketch_text.stroke-131");var subQ56=sQuery(id+"F2.wireOp",EDGE,"E1.sketch_text.stroke-130");var subQ57=sQuery(id+"F2.wireOp",EDGE,"E1.sketch_text.stroke-129");var subQ58=sQuery(id+"F2.wireOp",EDGE,"E1.sketch_text.stroke-128");var subQ59=sQuery(id+"F2.wireOp",EDGE,"E1.sketch_text.stroke-127");var subQ60=sQuery(id+"F2.wireOp",EDGE,"E1.sketch_text.stroke-126");var subQ61=sQuery(id+"F2.wireOp",EDGE,"E1.sketch_text.stroke-122");var subQ62=sQuery(id+"F2.wireOp",EDGE,"E1.sketch_text.stroke-121");var subQ63=sQuery(id+"F2.wireOp",EDGE,"E1.sketch_text.stroke-120");var subQ64=sQuery(id+"F2.wireOp",EDGE,"E1.sketch_text.stroke-119");var subQ65=sQuery(id+"F2.wireOp",EDGE,"E1.sketch_text.stroke-118");var subQ66=sQuery(id+"F2.wireOp",EDGE,"E1.sketch_text.stroke-117");var subQ67=sQuery(id+"F2.wireOp",EDGE,"E1.sketch_text.stroke-51");var subQ68=sQuery(id+"F2.wireOp",EDGE,"E1.sketch_text.stroke-50");var subQ69=sQuery(id+"F2.wireOp",EDGE,"E1.sketch_text.stroke-45");var subQ70=sQuery(id+"F2.wireOp",EDGE,"E1.sketch_text.stroke-226");var subQ71=sQuery(id+"F2.wireOp",EDGE,"E1.sketch_text.stroke-41");var subQ72=sQuery(id+"F2.wireOp",EDGE,"E1.sketch_text.stroke-225");var subQ73=sQuery(id+"F2.wireOp",EDGE,"E1.sketch_text.stroke-40");var subQ74=sQuery(id+"F2.wireOp",EDGE,"E1.sketch_text.stroke-224");var subQ75=sQuery(id+"F2.wireOp",EDGE,"E1.sketch_text.stroke-39");var subQ76=sQuery(id+"F2.wireOp",EDGE,"E1.sketch_text.stroke-223");var subQ77=sQuery(id+"F2.wireOp",EDGE,"E1.sketch_text.stroke-38");var subQ78=sQuery(id+"F2.wireOp",EDGE,"E1.sketch_text.stroke-222");var subQ79=sQuery(id+"F2.wireOp",EDGE,"E1.sketch_text.stroke-37");var subQ80=sQuery(id+"F2.wireOp",EDGE,"E1.sketch_text.stroke-221");var subQ81=sQuery(id+"F2.wireOp",EDGE,"E1.sketch_text.stroke-36");var subQ82=sQuery(id+"F2.wireOp",EDGE,"E1.sketch_text.stroke-220");var subQ83=sQuery(id+"F2.wireOp",EDGE,"E1.sketch_text.stroke-35");var subQ84=sQuery(id+"F2.wireOp",EDGE,"E1.sketch_text.stroke-216");var subQ85=sQuery(id+"F2.wireOp",EDGE,"E1.sketch_text.stroke-31");var subQ86=sQuery(id+"F2.wireOp",EDGE,"E1.sketch_text.stroke-215");var subQ87=sQuery(id+"F2.wireOp",EDGE,"E1.sketch_text.stroke-30");var subQ88=sQuery(id+"F2.wireOp",EDGE,"E1.sketch_text.stroke-214");var subQ89=sQuery(id+"F2.wireOp",EDGE,"E1.sketch_text.stroke-29");var subQ90=sQuery(id+"F2.wireOp",EDGE,"E1.sketch_text.stroke-28");var subQ91=sQuery(id+"F2.wireOp",EDGE,"E1.sketch_text.stroke-27");var subQ92=sQuery(id+"F2.wireOp",EDGE,"E1.sketch_text.stroke-211");var subQ93=sQuery(id+"F2.wireOp",EDGE,"E1.sketch_text.stroke-26");var subQ94=sQuery(id+"F2.wireOp",EDGE,"E1.sketch_text.stroke-210");var subQ95=sQuery(id+"F2.wireOp",EDGE,"E1.sketch_text.stroke-25");var subQ96=sQuery(id+"F2.wireOp",EDGE,"E1.sketch_text.stroke-116");var subQ97=sQuery(id+"F2.wireOp",EDGE,"E1.sketch_text.stroke-209");var subQ98=sQuery(id+"F2.wireOp",EDGE,"E1.sketch_text.stroke-24");var subQ99=sQuery(id+"F2.wireOp",EDGE,"E1.sketch_text.stroke-115");var subQ100=sQuery(id+"F2.wireOp",EDGE,"E1.sketch_text.stroke-208");var subQ101=sQuery(id+"F2.wireOp",EDGE,"E1.sketch_text.stroke-23");var subQ102=sQuery(id+"F2.wireOp",EDGE,"E1.sketch_text.stroke-114");var subQ103=sQuery(id+"F2.wireOp",EDGE,"E1.sketch_text.stroke-192");var subQ104=sQuery(id+"F2.wireOp",EDGE,"E1.sketch_text.stroke-7");var subQ105=sQuery(id+"F2.wireOp",EDGE,"E1.sketch_text.stroke-49");var subQ106=sQuery(id+"F2.wireOp",EDGE,"E1.sketch_text.stroke-4");var subQ107=sQuery(id+"F2.wireOp",EDGE,"E1.sketch_text.stroke-95");var subQ108=sQuery(id+"F2.wireOp",EDGE,"E1.sketch_text.stroke-48");var subQ109=sQuery(id+"F2.wireOp",EDGE,"E1.sketch_text.stroke-3");var subQ110=sQuery(id+"F2.wireOp",EDGE,"E1.sketch_text.stroke-94");var subQ111=sQuery(id+"F2.wireOp",EDGE,"E1.sketch_text.stroke-185");var subQ112=sQuery(id+"F2.wireOp",EDGE,"E1.sketch_text.stroke-0");var subQ113=sQuery(id+"F2.wireOp",EDGE,"E1.sketch_text.stroke-89");var subQ114=sQuery(id+"F2.wireOp",EDGE,"E1.sketch_text.stroke-164");var subQ115=sQuery(id+"F0.wireOp",EDGE,"E0.left");var subQ116=sQuery(id+"F2.wireOp",EDGE,"E1.sketch_text.stroke-77");var subQ117=sQuery(id+"F2.wireOp",EDGE,"E1.sketch_text.stroke-21");var subQ118=sQuery(id+"F2.wireOp",EDGE,"E1.sketch_text.stroke-112");var subQ119=sQuery(id+"F2.wireOp",EDGE,"E1.sketch_text.stroke-160");var subQ120=sQuery(id+"F0.wireOp",EDGE,"E0.bottom");var subQ121=sQuery(id+"F2.wireOp",EDGE,"E1.sketch_text.stroke-73");var subQ122=sQuery(id+"F2.wireOp",EDGE,"E1.sketch_text.stroke-202");var subQ123=sQuery(id+"F2.wireOp",EDGE,"E1.sketch_text.stroke-17");var subQ124=sQuery(id+"F2.wireOp",EDGE,"E1.sketch_text.stroke-47");var subQ125=sQuery(id+"F2.wireOp",EDGE,"E1.sketch_text.stroke-189");var subQ126=sQuery(id+"F2.wireOp",EDGE,"E1.sketch_text.stroke-2");var subQ127=sQuery(id+"F2.wireOp",EDGE,"E1.sketch_text.stroke-93");var subQ128=sQuery(id+"F2.wireOp",EDGE,"E1.sketch_text.stroke-165");var subQ129=sQuery(id+"F0.wireOp",EDGE,"E0.right");var subQ130=sQuery(id+"F2.wireOp",EDGE,"E1.sketch_text.stroke-78");var subQ131=sQuery(id+"F2.wireOp",EDGE,"E1.sketch_text.stroke-207");var subQ132=sQuery(id+"F2.wireOp",EDGE,"E1.sketch_text.stroke-22");var subQ133=sQuery(id+"F2.wireOp",EDGE,"E1.sketch_text.stroke-113");var subQ134=sQuery(id+"F2.wireOp",EDGE,"E1.sketch_text.stroke-163");var subQ135=sQuery(id+"F0.wireOp",EDGE,"E0.top");var subQ136=sQuery(id+"F2.wireOp",EDGE,"E1.sketch_text.stroke-76");var subQ137=sQuery(id+"F2.wireOp",EDGE,"E1.sketch_text.stroke-20");var subQ138=sQuery(id+"F2.wireOp",EDGE,"E1.sketch_text.stroke-111");var subQ139=sQuery(id+"F2.wireOp",EDGE,"E1.sketch_text.stroke-46");var subQ140=sQuery(id+"F2.wireOp",EDGE,"E1.sketch_text.stroke-188");var subQ141=sQuery(id+"F2.wireOp",EDGE,"E1.sketch_text.stroke-1");var subQ142=sQuery(id+"F2.wireOp",EDGE,"E1.sketch_text.stroke-92");var subQ143=sQuery(id+"F2.wireOp",EDGE,"E1.sketch_text.stroke-193");var subQ144=sQuery(id+"F2.wireOp",EDGE,"E1.sketch_text.stroke-8");var subQ145=sQuery(id+"F2.wireOp",EDGE,"E1.sketch_text.stroke-239");var subQ146=sQuery(id+"F2.wireOp",EDGE,"E1.sketch_text.stroke-52");var subQ147=sQuery(id+"F2.wireOp",EDGE,"E1.sketch_text.stroke-9");var subQ148=sQuery(id+"F2.wireOp",EDGE,"E1.sketch_text.stroke-100");var subQ149=sQuery(id+"F2.wireOp",EDGE,"E1.sketch_text.stroke-10");var subQ150=sQuery(id+"F2.wireOp",EDGE,"E1.sketch_text.stroke-101");var subQ151=sQuery(id+"F2.wireOp",EDGE,"E1.sketch_text.stroke-199");var subQ152=sQuery(id+"F2.wireOp",EDGE,"E1.sketch_text.stroke-14");var subQ153=sQuery(id+"F2.wireOp",EDGE,"E1.sketch_text.stroke-105");var subQ154=sQuery(id+"F2.wireOp",EDGE,"E1.sketch_text.stroke-200");var subQ155=sQuery(id+"F2.wireOp",EDGE,"E1.sketch_text.stroke-15");var subQ156=sQuery(id+"F2.wireOp",EDGE,"E1.sketch_text.stroke-106");var subQ157=sQuery(id+"F2.wireOp",EDGE,"E1.sketch_text.stroke-201");var subQ158=sQuery(id+"F2.wireOp",EDGE,"E1.sketch_text.stroke-16");var subQ159=sQuery(id+"F2.wireOp",EDGE,"E1.sketch_text.stroke-203");var subQ160=sQuery(id+"F2.wireOp",EDGE,"E1.sketch_text.stroke-18");var subQ161=sQuery(id+"F2.wireOp",EDGE,"E1.sketch_text.stroke-19");var subQ162=sQuery(id+"F2.wireOp",EDGE,"E1.sketch_text.stroke-110");var subQ163=sQuery(id+"F2.wireOp",EDGE,"E1.sketch_text.stroke-53");var subQ164=sQuery(id+"F2.wireOp",EDGE,"E1.sketch_text.stroke-59");var subQ165=sQuery(id+"F2.wireOp",EDGE,"E1.sketch_text.stroke-247");var subQ166=sQuery(id+"F2.wireOp",EDGE,"E1.sketch_text.stroke-60");var subQ167=sQuery(id+"F2.wireOp",EDGE,"E1.sketch_text.stroke-248");var subQ168=sQuery(id+"F2.wireOp",EDGE,"E1.sketch_text.stroke-61");var subQ169=sQuery(id+"F2.wireOp",EDGE,"E1.sketch_text.stroke-249");var subQ170=sQuery(id+"F2.wireOp",EDGE,"E1.sketch_text.stroke-62");var subQ171=sQuery(id+"F2.wireOp",EDGE,"E1.sketch_text.stroke-250");var subQ172=sQuery(id+"F2.wireOp",EDGE,"E1.sketch_text.stroke-63");var subQ173=sQuery(id+"F2.wireOp",EDGE,"E1.sketch_text.stroke-251");var subQ174=sQuery(id+"F2.wireOp",EDGE,"E1.sketch_text.stroke-64");var subQ175=sQuery(id+"F2.wireOp",EDGE,"E1.sketch_text.stroke-65");var subQ176=sQuery(id+"F2.wireOp",EDGE,"E1.sketch_text.stroke-66");var subQ177=sQuery(id+"F2.wireOp",EDGE,"E1.sketch_text.stroke-67");var subQ178=sQuery(id+"F2.wireOp",EDGE,"E1.sketch_text.stroke-68");var subQ179=sQuery(id+"F2.wireOp",EDGE,"E1.sketch_text.stroke-69");var subQ180=sQuery(id+"F2.wireOp",EDGE,"E1.sketch_text.stroke-70");var subQ181=sQuery(id+"F2.wireOp",EDGE,"E1.sketch_text.stroke-71");var subQ182=sQuery(id+"F2.wireOp",EDGE,"E1.sketch_text.stroke-72");var subQ183=sQuery(id+"F2.wireOp",EDGE,"E1.sketch_text.stroke-74");var subQ184=sQuery(id+"F2.wireOp",EDGE,"E1.sketch_text.stroke-75");var subQ185=sQuery(id+"F2.wireOp",EDGE,"E1.sketch_text.stroke-79");var subQ186=sQuery(id+"F2.wireOp",EDGE,"E1.sketch_text.stroke-80");var subQ187=sQuery(id+"F2.wireOp",EDGE,"E1.sketch_text.stroke-81");var subQ188=sQuery(id+"F2.wireOp",EDGE,"E1.sketch_text.stroke-82");var subQ189=sQuery(id+"F2.wireOp",EDGE,"E1.sketch_text.stroke-83");var subQ190=sQuery(id+"F2.wireOp",EDGE,"E1.sketch_text.stroke-84");var subQ191=sQuery(id+"F2.wireOp",EDGE,"E1.sketch_text.stroke-85");var subQ192=sQuery(id+"F2.wireOp",EDGE,"E1.sketch_text.stroke-90");var subQ193=sQuery(id+"F2.wireOp",EDGE,"E1.sketch_text.stroke-91");var subQ194=sQuery(id+"F2.wireOp",EDGE,"E1.sketch_text.stroke-96");var subQ195=sQuery(id+"F2.wireOp",EDGE,"E1.sketch_text.stroke-102");var subQ196=sQuery(id+"F2.wireOp",EDGE,"E1.sketch_text.stroke-103");var subQ197=sQuery(id+"F2.wireOp",EDGE,"E1.sketch_text.stroke-104");var subQ198=sQuery(id+"F2.wireOp",EDGE,"E1.sketch_text.stroke-252");var subQ199=sQuery(id+"F2.wireOp",EDGE,"E1.sketch_text.stroke-253");var subQ200=sQuery(id+"F2.wireOp",EDGE,"E1.sketch_text.stroke-254");Q0=makeQuery(id+"F8.boolean.opBoolean","SPLIT",FACE,{"disambiguationData":[TD([makeQuery(id+"F1.opExtrude","SWEPT_FACE",FACE,{"disambiguationData":[OSD([subQ120])]})])],"derivedFrom":makeQuery(id+"F3.boolean.opBoolean","MERGE",FACE,{"derivedFrom":[makeQuery(id+"F1.opExtrude","CAP_FACE",FACE,{"disambiguationData":[OSD([subQ120,subQ135,subQ115,subQ129])],"isStart":true}),makeQuery(id+"F3.opExtrude","CAP_FACE",FACE,{"disambiguationData":[OSD([subQ112,subQ141,subQ126,subQ109,subQ106,sQuery(id+"F2.wireOp",EDGE,"E1.sketch_text.stroke-5"),sQuery(id+"F2.wireOp",EDGE,"E1.sketch_text.stroke-6"),subQ104,subQ144,subQ147,subQ149,sQuery(id+"F2.wireOp",EDGE,"E1.sketch_text.stroke-11"),sQuery(id+"F2.wireOp",EDGE,"E1.sketch_text.stroke-12"),sQuery(id+"F2.wireOp",EDGE,"E1.sketch_text.stroke-13"),subQ152,subQ155,subQ158,subQ123,subQ160,subQ161,subQ137,subQ117,subQ132,subQ101,subQ98,subQ95])],"isStart":true}),makeQuery(id+"F3.opExtrude","CAP_FACE",FACE,{"disambiguationData":[OSD([subQ93,subQ91,subQ90,subQ89,subQ87,subQ85,sQuery(id+"F2.wireOp",EDGE,"E1.sketch_text.stroke-32"),sQuery(id+"F2.wireOp",EDGE,"E1.sketch_text.stroke-33"),sQuery(id+"F2.wireOp",EDGE,"E1.sketch_text.stroke-34"),subQ83,subQ81,subQ79,subQ77,subQ75,subQ73,subQ71,sQuery(id+"F2.wireOp",EDGE,"E1.sketch_text.stroke-42"),sQuery(id+"F2.wireOp",EDGE,"E1.sketch_text.stroke-43"),sQuery(id+"F2.wireOp",EDGE,"E1.sketch_text.stroke-44"),subQ69,subQ139,subQ124,subQ108,subQ105,subQ68])],"isStart":true}),makeQuery(id+"F3.opExtrude","CAP_FACE",FACE,{"disambiguationData":[OSD([subQ67,subQ146,subQ163,sQuery(id+"F2.wireOp",EDGE,"E1.sketch_text.stroke-54"),sQuery(id+"F2.wireOp",EDGE,"E1.sketch_text.stroke-55"),sQuery(id+"F2.wireOp",EDGE,"E1.sketch_text.stroke-56"),sQuery(id+"F2.wireOp",EDGE,"E1.sketch_text.stroke-57"),sQuery(id+"F2.wireOp",EDGE,"E1.sketch_text.stroke-58"),subQ164,subQ166,subQ168,subQ170,subQ172,subQ174,subQ175,subQ176,subQ177,subQ178,subQ179,subQ180,subQ181,subQ182,subQ121,subQ183,subQ184,subQ136,subQ116,subQ130])],"isStart":true}),makeQuery(id+"F3.opExtrude","CAP_FACE",FACE,{"disambiguationData":[OSD([subQ185,subQ186,subQ187,subQ188,subQ189,subQ190,subQ191,sQuery(id+"F2.wireOp",EDGE,"E1.sketch_text.stroke-86"),sQuery(id+"F2.wireOp",EDGE,"E1.sketch_text.stroke-87"),sQuery(id+"F2.wireOp",EDGE,"E1.sketch_text.stroke-88"),subQ113,subQ192,subQ193,subQ142,subQ127,subQ110,subQ107,subQ194,sQuery(id+"F2.wireOp",EDGE,"E1.sketch_text.stroke-97"),sQuery(id+"F2.wireOp",EDGE,"E1.sketch_text.stroke-98"),sQuery(id+"F2.wireOp",EDGE,"E1.sketch_text.stroke-99"),subQ148,subQ150,subQ195,subQ196,subQ197,subQ153,subQ156,sQuery(id+"F2.wireOp",EDGE,"E1.sketch_text.stroke-107"),sQuery(id+"F2.wireOp",EDGE,"E1.sketch_text.stroke-108"),sQuery(id+"F2.wireOp",EDGE,"E1.sketch_text.stroke-109"),subQ162,subQ138,subQ118,subQ133,subQ102,subQ99])],"isStart":true}),makeQuery(id+"F3.opExtrude","CAP_FACE",FACE,{"disambiguationData":[OSD([subQ96,subQ66,subQ65,subQ64,subQ63,subQ62,subQ61,sQuery(id+"F2.wireOp",EDGE,"E1.sketch_text.stroke-123"),sQuery(id+"F2.wireOp",EDGE,"E1.sketch_text.stroke-124"),sQuery(id+"F2.wireOp",EDGE,"E1.sketch_text.stroke-125"),subQ60,subQ59,subQ58,subQ57,subQ56,subQ55,subQ54,subQ53,sQuery(id+"F2.wireOp",EDGE,"E1.sketch_text.stroke-134"),sQuery(id+"F2.wireOp",EDGE,"E1.sketch_text.stroke-135"),sQuery(id+"F2.wireOp",EDGE,"E1.sketch_text.stroke-136"),subQ52,subQ51,subQ50,subQ49,subQ48,subQ47,subQ46,sQuery(id+"F2.wireOp",EDGE,"E1.sketch_text.stroke-144"),sQuery(id+"F2.wireOp",EDGE,"E1.sketch_text.stroke-145"),sQuery(id+"F2.wireOp",EDGE,"E1.sketch_text.stroke-146"),subQ45,subQ44,subQ43,subQ42,subQ41,subQ40])],"isStart":true}),makeQuery(id+"F3.opExtrude","CAP_FACE",FACE,{"disambiguationData":[OSD([subQ39,subQ38,subQ37,subQ36,subQ35,subQ34,subQ33,subQ119,subQ32,subQ31,subQ134,subQ114,subQ128,subQ30,subQ29,subQ28])],"isStart":true}),makeQuery(id+"F3.opExtrude","CAP_FACE",FACE,{"disambiguationData":[OSD([subQ27,sQuery(id+"F2.wireOp",EDGE,"E1.sketch_text.stroke-170"),subQ26,subQ25,subQ24,subQ23,subQ22,subQ21,subQ20,subQ19,subQ18,subQ17,subQ16,subQ15,subQ14,subQ13,subQ111,sQuery(id+"F2.wireOp",EDGE,"E1.sketch_text.stroke-186"),sQuery(id+"F2.wireOp",EDGE,"E1.sketch_text.stroke-187"),subQ140])],"isStart":true}),makeQuery(id+"F3.opExtrude","CAP_FACE",FACE,{"disambiguationData":[OSD([subQ125,subQ12,subQ11,subQ103,subQ143,sQuery(id+"F2.wireOp",EDGE,"E1.sketch_text.stroke-194"),sQuery(id+"F2.wireOp",EDGE,"E1.sketch_text.stroke-195"),sQuery(id+"F2.wireOp",EDGE,"E1.sketch_text.stroke-196"),subQ10,subQ9,subQ151,subQ154,subQ157,subQ122,subQ159,sQuery(id+"F2.wireOp",EDGE,"E1.sketch_text.stroke-204"),sQuery(id+"F2.wireOp",EDGE,"E1.sketch_text.stroke-205"),sQuery(id+"F2.wireOp",EDGE,"E1.sketch_text.stroke-206"),subQ131,subQ100,subQ97,subQ94,subQ92,subQ8])],"isStart":true}),makeQuery(id+"F3.opExtrude","CAP_FACE",FACE,{"disambiguationData":[OSD([subQ7,subQ88,subQ86,subQ84,subQ6,subQ5,subQ4,subQ82,subQ80,subQ78,subQ76,subQ74,subQ72,subQ70,subQ3,subQ2,subQ1,sQuery(id+"F2.wireOp",EDGE,"E1.sketch_text.stroke-230"),sQuery(id+"F2.wireOp",EDGE,"E1.sketch_text.stroke-231"),sQuery(id+"F2.wireOp",EDGE,"E1.sketch_text.stroke-232"),sQuery(id+"F2.wireOp",EDGE,"E1.sketch_text.stroke-233"),sQuery(id+"F2.wireOp",EDGE,"E1.sketch_text.stroke-234"),sQuery(id+"F2.wireOp",EDGE,"E1.sketch_text.stroke-235"),sQuery(id+"F2.wireOp",EDGE,"E1.sketch_text.stroke-236"),sQuery(id+"F2.wireOp",EDGE,"E1.sketch_text.stroke-237"),subQ0,subQ145,sQuery(id+"F2.wireOp",EDGE,"E1.sketch_text.stroke-240"),sQuery(id+"F2.wireOp",EDGE,"E1.sketch_text.stroke-241"),sQuery(id+"F2.wireOp",EDGE,"E1.sketch_text.stroke-242"),sQuery(id+"F2.wireOp",EDGE,"E1.sketch_text.stroke-243"),sQuery(id+"F2.wireOp",EDGE,"E1.sketch_text.stroke-244"),sQuery(id+"F2.wireOp",EDGE,"E1.sketch_text.stroke-245"),sQuery(id+"F2.wireOp",EDGE,"E1.sketch_text.stroke-246"),subQ165,subQ167,subQ169,subQ171,subQ173,subQ198,subQ199,subQ200])],"isStart":true})]})});}
            var sketch = newSketch(context, id + "F10", { "sketchPlane" : qUnion([Q0])});
            skLineSegment(sketch, "E4", {"start": v(48.17, -13.86) * mm, "end": v(47.6, -15.55) * mm});
            skLineSegment(sketch, "E5", {"start": v(47.6, -15.55) * mm, "end": v(55.4, -15.55) * mm});
            skLineSegment(sketch, "E6", {"start": v(55.4, -15.55) * mm, "end": v(54.72, -13.84) * mm});
            skLineSegment(sketch, "E7", {"start": v(54.72, -13.84) * mm, "end": v(48.17, -13.86) * mm});
            skSolve(sketch);
        }
        {
            var Q0;
            Q0 = qSketchRegion(id + "F10", true);
            extrude(context, id + "F11", {"entities" : qUnion([Q0]), "operationType" : NewBodyOperationType.ADD, "oppositeDirection" : true, "depth" : 5.08 * mm});
        }
    });
